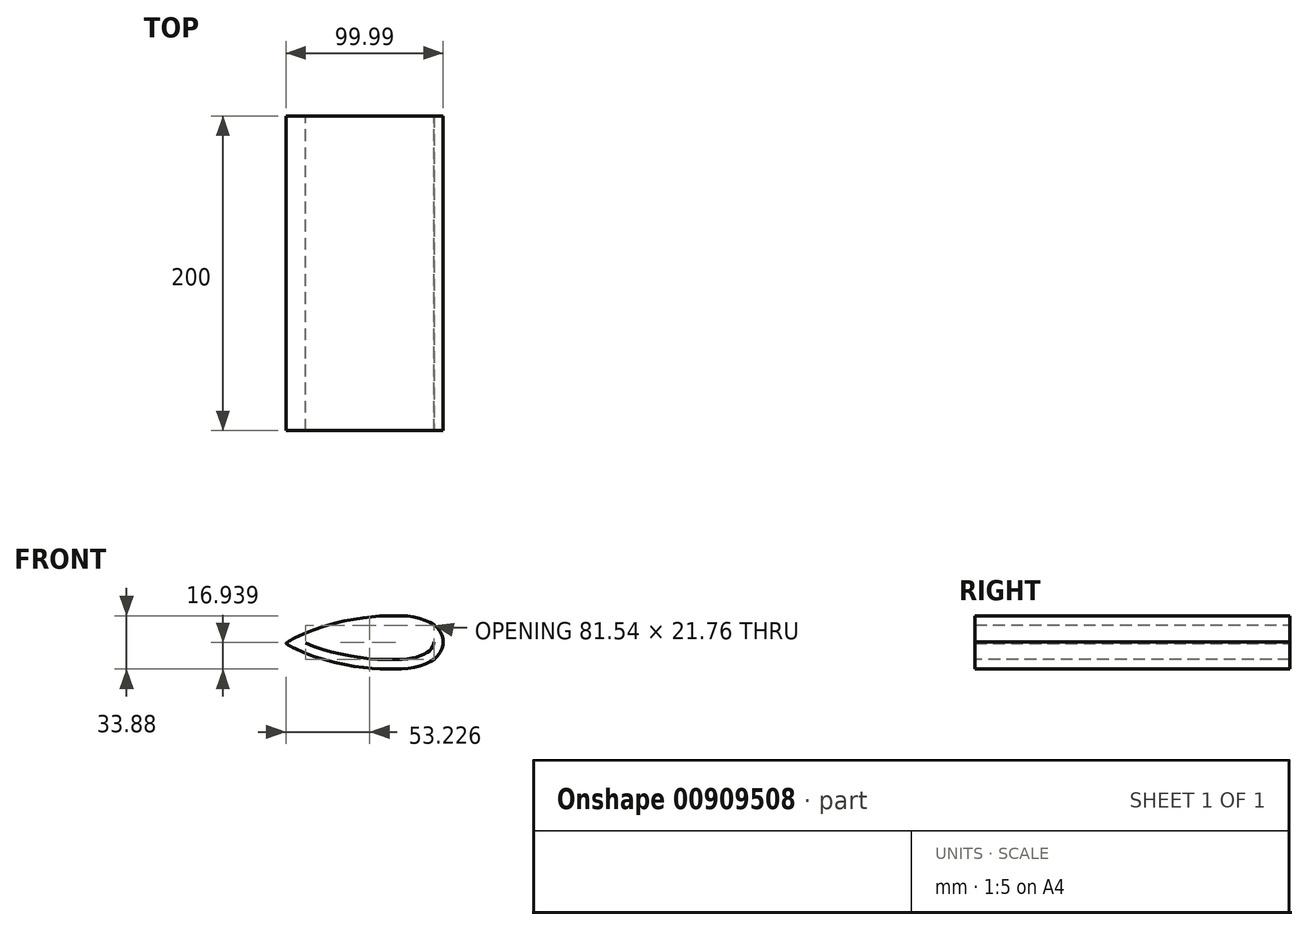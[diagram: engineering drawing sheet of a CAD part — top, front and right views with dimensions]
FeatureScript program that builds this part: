
annotation { "Feature Type Name" : "Feature", "Feature Type Description" : "" }
export const myFeature = defineFeature(function(context is Context, id is Id, definition is map)
    precondition{}
    {
        {
            var Q0;
            Q0=qCreatedBy(makeId("Front.planeOp"),FACE);
            var sketch = newSketch(context, id + "F0", { "sketchPlane" : qUnion([Q0])});
            skFitSpline(sketch, "E0", {"points": [v(-56.66, -0.49) * mm, v(-29.02, 11.29) * mm, v(-1.4, 16.48) * mm, v(15.1, 17.01) * mm, v(27, 15.78) * mm, v(36.04, 12.06) * mm, v(40.32, 8.33) * mm, v(42.98, 3.38) * mm, v(43.33, 0.42) * mm], "startDerivative": vector(96, 70.54) * mm, "endDerivative": vector(0.85, -43.4) * mm});
            skFitSpline(sketch, "E1.MirrorCS", {"points": [v(-56.66, -0.49) * mm, v(-28.81, -11.76) * mm, v(-1.1, -16.45) * mm, v(15.4, -16.68) * mm, v(27.28, -15.23) * mm, v(36.26, -11.35) * mm, v(40.47, -7.54) * mm, v(43.04, -2.54) * mm, v(43.33, 0.42) * mm], "startDerivative": vector(97.27, -68.79) * mm, "endDerivative": vector(0.07, 43.4) * mm});
            skFitSpline(sketch, "E2.0", {"points": [v(-53.1, -5.32) * mm, v(-52.31, -4.74) * mm, v(-50.42, -3.5) * mm, v(-46.86, -1.6) * mm, v(-42.76, 0.25) * mm, v(-38.28, 2.02) * mm, v(-33.56, 3.66) * mm, v(-28.74, 5.15) * mm, v(-23.98, 6.46) * mm, v(-17.78, 7.95) * mm, v(-11.82, 9.1) * mm, v(-6.21, 9.92) * mm, v(-2.2, 10.4) * mm, v(1.57, 10.72) * mm, v(5.14, 10.93) * mm, v(8.53, 11.04) * mm, v(11.24, 11.06) * mm, v(13.35, 11.04) * mm, v(14.65, 11.02) * mm, v(15.68, 11) * mm, v(16.68, 10.97) * mm, v(18.4, 10.9) * mm, v(20.24, 10.79) * mm, v(21.97, 10.6) * mm, v(23.23, 10.43) * mm, v(24.23, 10.25) * mm, v(25.01, 10.08) * mm, v(25.59, 9.95) * mm, v(26.16, 9.8) * mm, v(26.93, 9.58) * mm, v(27.88, 9.27) * mm, v(29, 8.86) * mm, v(30.07, 8.42) * mm, v(31.08, 7.95) * mm, v(32, 7.47) * mm, v(32.7, 7.08) * mm, v(33.18, 6.78) * mm, v(33.62, 6.5) * mm, v(34.09, 6.16) * mm, v(34.55, 5.78) * mm, v(34.95, 5.4) * mm, v(35.27, 5.04) * mm, v(35.53, 4.71) * mm, v(35.8, 4.35) * mm, v(36.16, 3.85) * mm, v(36.54, 3.2) * mm, v(36.82, 2.7) * mm, v(36.99, 2.32) * mm, v(37.1, 2.07) * mm, v(37.17, 1.86) * mm, v(37.21, 1.73) * mm, v(37.23, 1.66) * mm, v(37.25, 1.6) * mm, v(37.27, 1.51) * mm, v(37.28, 1.4) * mm, v(37.3, 1.23) * mm, v(37.32, 0.93) * mm, v(37.33, 0.54) * mm, v(37.34, 0.3) * mm]});
            skFitSpline(sketch, "E2.1", {"points": [v(-53.2, 4.41) * mm, v(-52.39, 3.84) * mm, v(-50.47, 2.64) * mm, v(-46.88, 0.81) * mm, v(-42.75, -0.97) * mm, v(-38.23, -2.66) * mm, v(-33.49, -4.22) * mm, v(-28.64, -5.62) * mm, v(-23.86, -6.84) * mm, v(-17.63, -8.22) * mm, v(-11.66, -9.25) * mm, v(-6.03, -9.98) * mm, v(-2.02, -10.38) * mm, v(1.77, -10.64) * mm, v(5.34, -10.79) * mm, v(8.73, -10.83) * mm, v(11.44, -10.8) * mm, v(13.55, -10.75) * mm, v(14.85, -10.7) * mm, v(15.88, -10.66) * mm, v(16.88, -10.61) * mm, v(18.59, -10.52) * mm, v(20.43, -10.37) * mm, v(22.16, -10.15) * mm, v(23.41, -9.95) * mm, v(24.41, -9.76) * mm, v(25.2, -9.58) * mm, v(25.76, -9.43) * mm, v(26.33, -9.27) * mm, v(27.1, -9.04) * mm, v(28.04, -8.71) * mm, v(29.15, -8.28) * mm, v(30.22, -7.81) * mm, v(31.22, -7.33) * mm, v(32.14, -6.83) * mm, v(32.82, -6.43) * mm, v(33.3, -6.12) * mm, v(33.73, -5.83) * mm, v(34.2, -5.48) * mm, v(34.64, -5.1) * mm, v(35.04, -4.7) * mm, v(35.36, -4.34) * mm, v(35.61, -4.01) * mm, v(35.88, -3.65) * mm, v(36.22, -3.14) * mm, v(36.6, -2.5) * mm, v(36.86, -1.97) * mm, v(37.02, -1.6) * mm, v(37.13, -1.34) * mm, v(37.2, -1.13) * mm, v(37.24, -1) * mm, v(37.26, -0.93) * mm, v(37.27, -0.86) * mm, v(37.29, -0.78) * mm, v(37.3, -0.67) * mm, v(37.32, -0.5) * mm, v(37.33, -0.2) * mm, v(37.33, 0.2) * mm, v(37.33, 0.43) * mm]});
            skSolve(sketch);
        }
        {
            var Q0;
            Q0=qSketchRegion(id+"F0",true);
            extrude(context, id + "F1", {"entities" : qUnion([Q0]), "depth" : 200 * mm, "offsetDistance" : 25 * mm});
        }
    });
